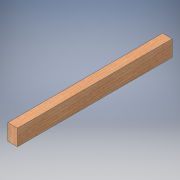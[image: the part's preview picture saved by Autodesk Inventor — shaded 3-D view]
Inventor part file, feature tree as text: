
AUTODESK INVENTOR PART (.ipt)
format: ipt  version: 2016 SP1 (Build 200210100, 210)  size: 99,840 bytes
history: native  units: in
note: dims shown in document units (in); Inventor stores cm internally (conversion verified against a paired STEP export)
features: extrude x1, sketch x1
ambient origin geometry x8: Origin, YZ Plane, XZ Plane, XY Plane, X Axis, Y Axis, Z Axis, Center Point
bodies: Solid1 (feature_tree)
feature tree (2):
  extrude  "Extrusion1"  Depth=2.5in
  sketch  "Sketch1"  dims[d0=1.5in d1=2.5in d2=24.0in d3=0.0in]
